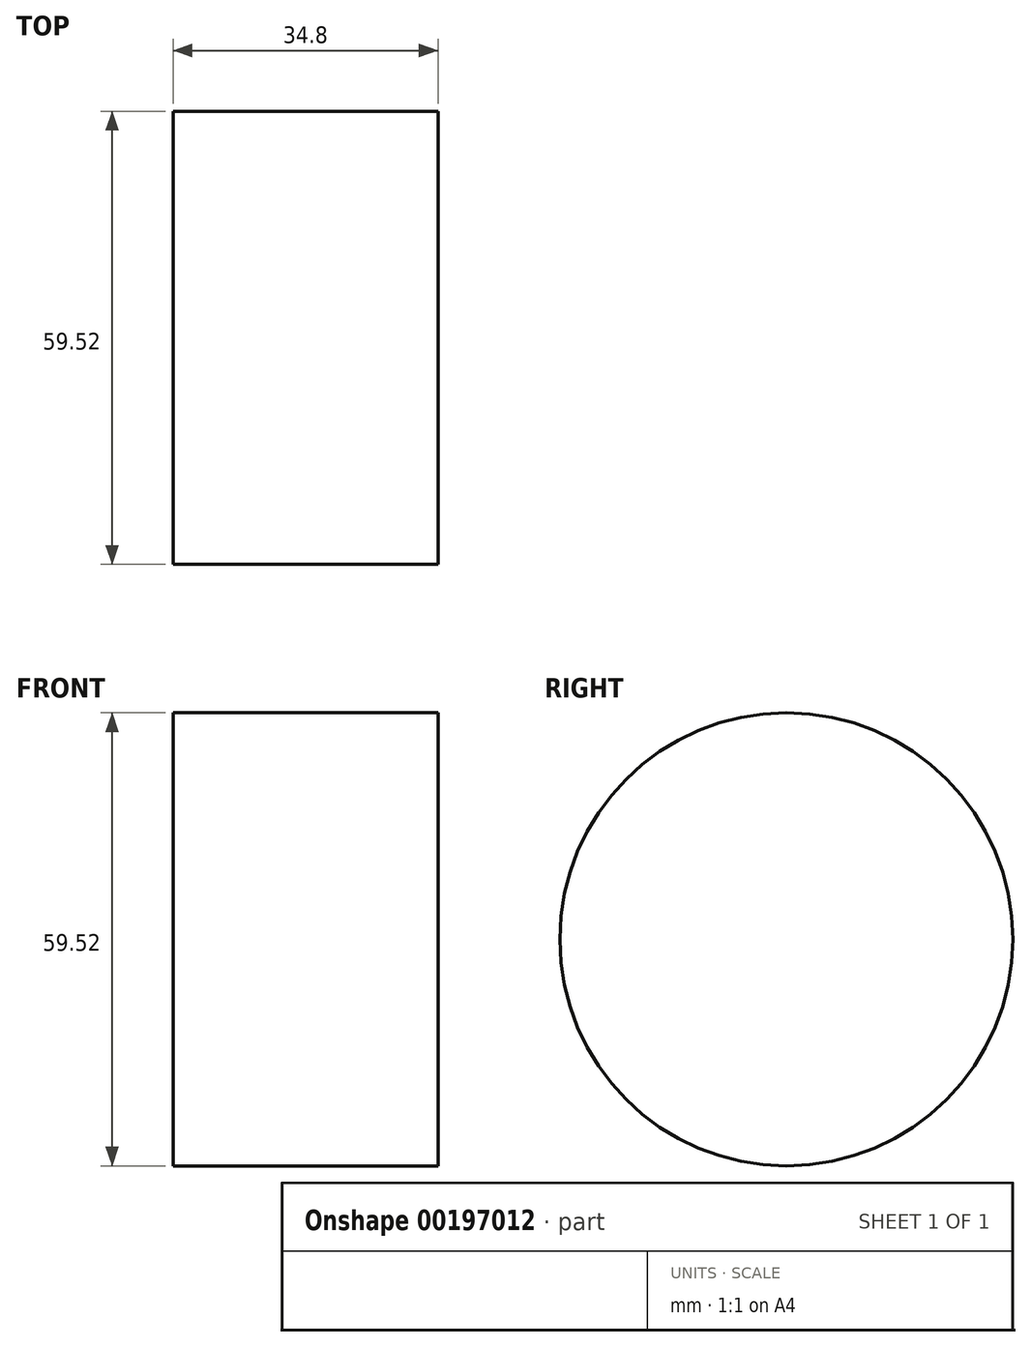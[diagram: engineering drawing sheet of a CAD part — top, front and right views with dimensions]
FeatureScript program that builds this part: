
annotation { "Feature Type Name" : "Feature", "Feature Type Description" : "" }
export const myFeature = defineFeature(function(context is Context, id is Id, definition is map)
    precondition{}
    {
        {
            var Q0;
            Q0=qCreatedBy(makeId("Right.planeOp"),FACE);
            var sketch = newSketch(context, id + "F0", { "sketchPlane" : qUnion([Q0])});
            skCircle(sketch, "E0", {"center": v(0, 0) * mm, "radius": 29.76 * mm});
            skSolve(sketch);
        }
        {
            var Q0;
            Q0 = qSketchRegion(id + "F0", true);
            extrude(context, id + "F1", {"entities" : qUnion([Q0]), "oppositeDirection" : true, "depth" : 34.8 * mm});
        }
    });
